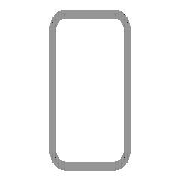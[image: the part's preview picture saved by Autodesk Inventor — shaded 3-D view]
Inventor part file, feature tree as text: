
AUTODESK INVENTOR PART (.ipt)
format: ipt  version: 2025 (Build 290162010, 162A)  size: 148,992 bytes
history: native  units: mm (DEFAULTED — no unit token found)
features: other x3, sketch x2, extrude x1, plane x1
ambient origin geometry x8: Origin, YZ Plane, XZ Plane, XY Plane, X Axis, Y Axis, Z Axis, Center Point
bodies: Solid1 (feature_tree), Body (feature_tree)
feature tree (7):
  other  "Driven Length"
  other  "Start plane"
  other  "End plane"
  extrude  "Extrusion2"  TaperAngle=0.0deg  [1 undecoded]
  sketch  "Sketch3"  dims[d3=4382.0mm d4=0.0mm]
  plane  "Work Plane3"
  sketch  "Sketch5"  dims[d7=4.0mm d9=20.0mm d11=40.0mm d12=2.0mm d13=-0.0mm d14=4382.0mm d15=10.0mm d16=20.0mm d17=90.0deg d18=4382.0mm d19=5.846853mm d20=0.0mm d21=0.0mm]
note: 1 required parameter value undecoded (feature->parameter linkage not recoverable at this tier; creation-order binding heuristic only, values carry confidence <= 0.55)
